# Revit family: BuroSeating_Konfurb Fly Sled
name_source: partatom
category: Furniture
units: mm (PartAtom-declared; Revit-internal decimal feet)

## family parameters
Always vertical = Yes
Cut with Voids When Loaded = No
OmniClass Number = 23.40.70.14.64.11
OmniClass Title = Office Furniture
Room Calculation Point = No
Shared = No
Work Plane-Based = No

## types (6) — shared parameters
ArmRestMaterial = BuroSeating_Polypropylene_Black
Assembly Code = E2020
BaseOffset = 18 mm  [stored 0.0590551 ft]
Manufacturer = Buro Seating
Model = KON332-x-0
NominalDepth = 500 mm  [stored 1.64042 ft]
NominalHeight = 845 mm  [stored 2.77231 ft]
NominalWidth = 460 mm  [stored 1.50919 ft]
ProductGroup = Konfurb Fly Sled
ProductPageURL AU = https://buroseating.com
ProductPageURL NZ = https://buroseating.co.nz
ProductRange = Konfurb
SeatHeight = 450 mm  [stored 1.47638 ft]
URL = https://buroseating.co.nz
URL AU = https://buroseating.com
WarrantyDescription = Full 5 year guarantee (excluding upholstery)
zero-valued in all types: Default Elevation

## per-type parameters (varying)
| type | Description | SeatArms | SeatCushion | Shell | Upholstery |
| Fly Sled Chair - Shell | Konfurb Fly Sled Base Shell Chair | No | No | Yes | No |
| Fly Sled Chair - Shell w Arms | Konfurb Fly Sled Base Shell Chair with Arms | Yes | No | Yes | No |
| Fly Sled Chair - Shell w Arms and Cushion | Konfurb Fly Sled Base Shell Chair with Arms and Cushion | Yes | Yes | Yes | No |
| Fly Sled Chair - Shell w Cushion | Konfurb Fly Sled Base Shell Chair with Cushion | No | Yes | Yes | No |
| Fly Sled Chair - Fabric | Konfurb Fly Sled Base Fabric Chair | No | No | No | Yes |
| Fly Sled Chair - Fabric w Arms | Konfurb Fly Sled Base Fabric Chair with Arms | Yes | No | No | Yes |

note: [stored X ft] marks values corroborated as IEEE doubles in the binary element streams (Revit-internal decimal feet)

## geometry (parser evidence)
native form markers: Sweep x8
no freeform markers — native parametric forms only
